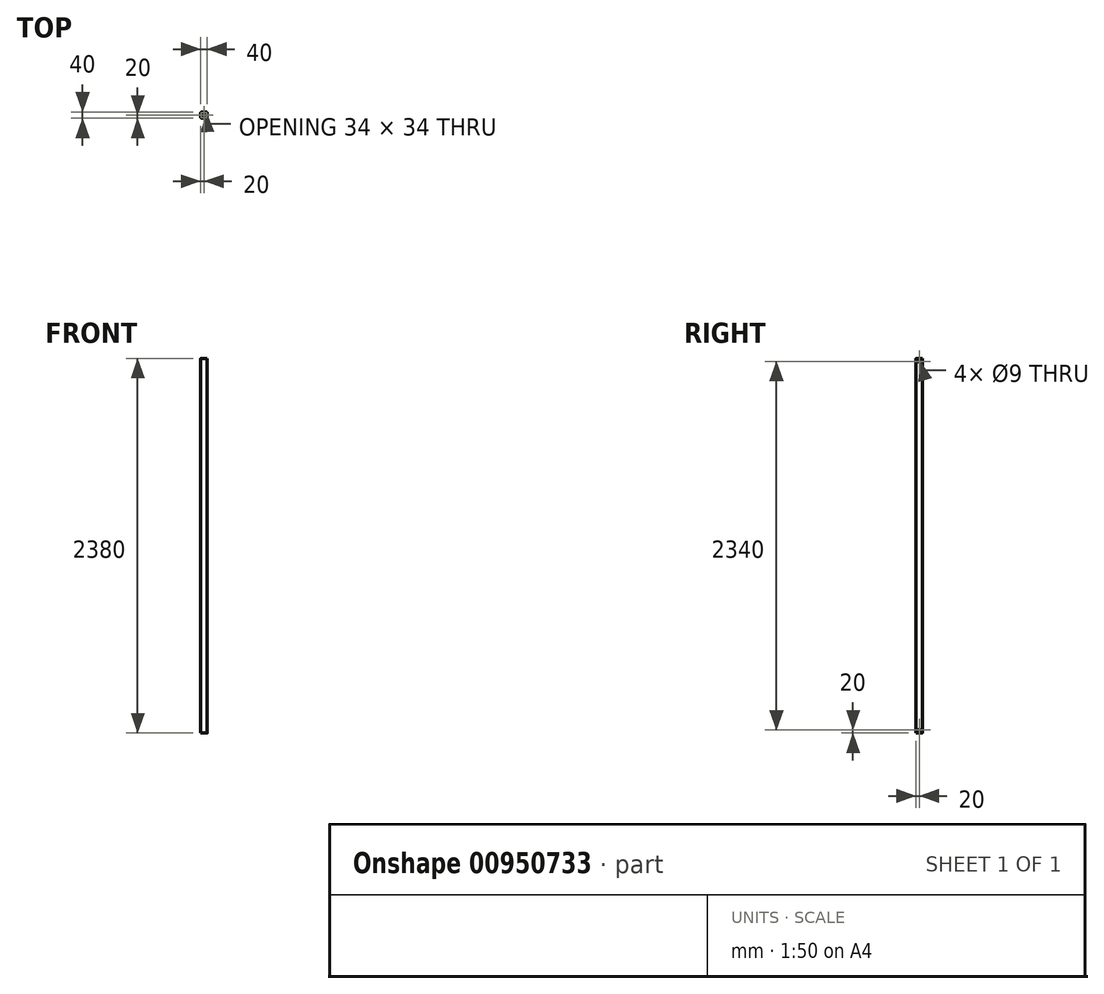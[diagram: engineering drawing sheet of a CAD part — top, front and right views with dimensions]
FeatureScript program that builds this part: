
annotation { "Feature Type Name" : "Feature", "Feature Type Description" : "" }
export const myFeature = defineFeature(function(context is Context, id is Id, definition is map)
    precondition{}
    {
        {
            var Q0;
            Q0=qCreatedBy(makeId("Top.planeOp"),FACE);
            var sketch = newSketch(context, id + "F0", { "sketchPlane" : qUnion([Q0])});
            skLineSegment(sketch, "E0.bottom", {"start": v(15.5, -20) * mm, "end": v(-15.5, -20) * mm});
            skLineSegment(sketch, "E0.top", {"start": v(15.5, 20) * mm, "end": v(-15.5, 20) * mm});
            skLineSegment(sketch, "E0.left", {"start": v(20, -15.5) * mm, "end": v(20, 15.5) * mm});
            skLineSegment(sketch, "E0.right", {"start": v(-20, -15.5) * mm, "end": v(-20, 15.5) * mm});
            skPoint(sketch, "E0.middle", {"position": v(0, 0) * mm});
            skPoint(sketch, "E1.visualSharp", {"position": v(-20, 20) * mm});
            skArc(sketch, "E2.filletArc", {"start": v(-15.5, 20) * mm, "mid": v(-18.68, 18.68) * mm, "end": v(-20, 15.5) * mm});
            skPoint(sketch, "E3.visualSharp", {"position": v(20, 20) * mm});
            skArc(sketch, "E3.filletArc", {"start": v(20, 15.5) * mm, "mid": v(18.68, 18.68) * mm, "end": v(15.5, 20) * mm});
            skPoint(sketch, "E4.visualSharp", {"position": v(20, -20) * mm});
            skArc(sketch, "E4.filletArc", {"start": v(15.5, -20) * mm, "mid": v(18.68, -18.68) * mm, "end": v(20, -15.5) * mm});
            skPoint(sketch, "E5.visualSharp", {"position": v(-20, -20) * mm});
            skArc(sketch, "E5.filletArc", {"start": v(-20, -15.5) * mm, "mid": v(-18.68, -18.68) * mm, "end": v(-15.5, -20) * mm});
            skArc(sketch, "E6.0", {"start": v(17, 15.5) * mm, "mid": v(16.56, 16.56) * mm, "end": v(15.5, 17) * mm});
            skLineSegment(sketch, "E6.1", {"start": v(17, -15.5) * mm, "end": v(17, 15.5) * mm});
            skLineSegment(sketch, "E6.2", {"start": v(15.5, 17) * mm, "end": v(-15.5, 17) * mm});
            skArc(sketch, "E6.3", {"start": v(15.5, -17) * mm, "mid": v(16.56, -16.56) * mm, "end": v(17, -15.5) * mm});
            skArc(sketch, "E6.4", {"start": v(-15.5, 17) * mm, "mid": v(-16.56, 16.56) * mm, "end": v(-17, 15.5) * mm});
            skLineSegment(sketch, "E6.5", {"start": v(-17, -15.5) * mm, "end": v(-17, 15.5) * mm});
            skArc(sketch, "E6.6", {"start": v(-17, -15.5) * mm, "mid": v(-16.56, -16.56) * mm, "end": v(-15.5, -17) * mm});
            skLineSegment(sketch, "E6.7", {"start": v(15.5, -17) * mm, "end": v(-15.5, -17) * mm});
            skSolve(sketch);
        }
        {
            var Q0;
            Q0=qSketchRegion(id+"F0",true);
            extrude(context, id + "F1", {"entities" : qUnion([Q0]), "depth" : (2460 - 80) * mm, "offsetDistance" : 25 * mm});
        }
        {
            var Q0;
            Q0=makeQuery(id+"F1.opExtrude","SWEPT_FACE",FACE,{"disambiguationData":[OSD([sQuery(id+"F0.wireOp",EDGE,"E0.left")])]});
            var sketch = newSketch(context, id + "F2", { "sketchPlane" : qUnion([Q0])});
            skLineSegment(sketch, "E7", {"start": v(0, 0) * mm, "end": v(0, 2380) * mm, "construction": true});
            skCircle(sketch, "E8", {"center": v(0, 2360) * mm, "radius": 4.5 * mm});
            skCircle(sketch, "E9", {"center": v(0, 20) * mm, "radius": 4.5 * mm});
            skSolve(sketch);
        }
        {
            var Q0;
            Q0=qSketchRegion(id+"F2",true);
            extrude(context, id + "F3", {"entities" : qUnion([Q0]), "operationType" : NewBodyOperationType.REMOVE, "endBound" : BoundingType.THROUGH_ALL, "oppositeDirection" : true, "depth" : 25 * mm, "offsetDistance" : 25 * mm});
        }
    });
